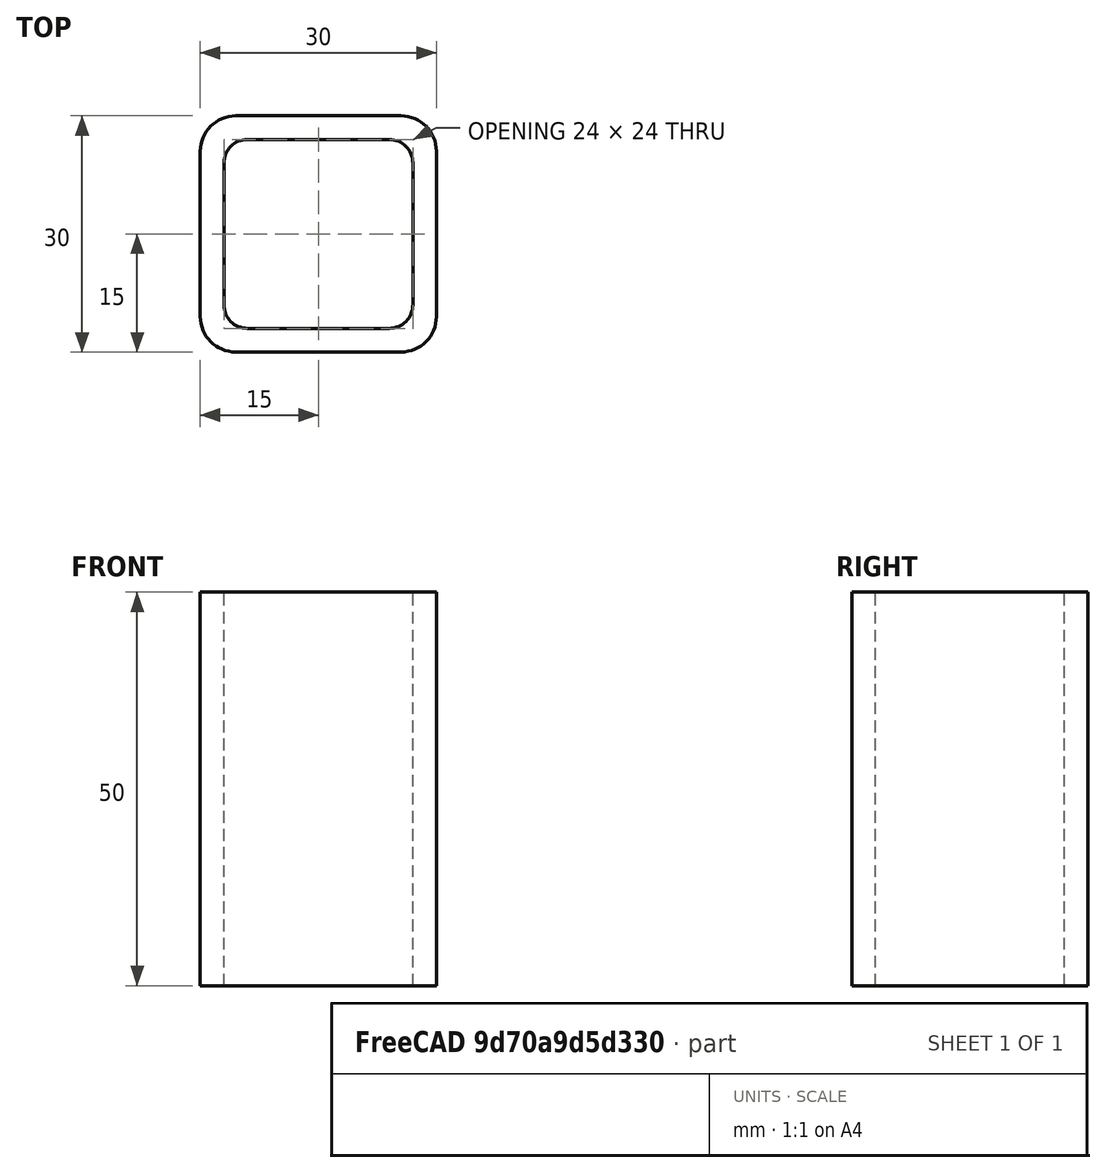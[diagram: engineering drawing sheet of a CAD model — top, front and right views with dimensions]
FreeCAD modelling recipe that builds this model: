
FCSTD DOCUMENT  (FreeCAD 0.15R4671 (Git))
Label: Square hollow section 30x30x3 EN10219 S235JRH
License: All rights reserved
LicenseURL: http://en.wikipedia.org/wiki/All_rights_reserved
objects: Sketcher::SketchObject×1, Part::Extrusion×1
note: 2 computed .brp shape members not serialized (recipe doc carries the construction recipe); baked Part::Feature solids carry a one-line shape summary decoded from their .brp

FEATURE [Sketcher::SketchObject] Sketch
  sketch-geometry (16):
    g0: LineSegment StartX=-9 StartY=12 StartZ=0 EndX=9 EndY=12 EndZ=0
    g1: LineSegment StartX=12 StartY=9 StartZ=0 EndX=12 EndY=-9 EndZ=0
    g2: LineSegment StartX=9 StartY=-12 StartZ=0 EndX=-9 EndY=-12 EndZ=0
    g3: LineSegment StartX=-12 StartY=-9 StartZ=0 EndX=-12 EndY=9 EndZ=0
    g4: LineSegment StartX=-10.5 StartY=15 StartZ=0 EndX=10.5 EndY=15 EndZ=0
    g5: LineSegment StartX=15 StartY=10.5 StartZ=0 EndX=15 EndY=-10.5 EndZ=0
    g6: LineSegment StartX=10.5 StartY=-15 StartZ=0 EndX=-10.5 EndY=-15 EndZ=0
    g7: LineSegment StartX=-15 StartY=-10.5 StartZ=0 EndX=-15 EndY=10.5 EndZ=0
    g8: ArcOfCircle CenterX=-9 CenterY=9 CenterZ=0 NormalX=0 NormalY=0 NormalZ=1 Radius=3 StartAngle=1.5708 EndAngle=3.14159
    g9: ArcOfCircle CenterX=9 CenterY=9 CenterZ=0 NormalX=0 NormalY=0 NormalZ=1 Radius=3 StartAngle=0 EndAngle=1.5708
    g10: ArcOfCircle CenterX=9 CenterY=-9 CenterZ=0 NormalX=0 NormalY=0 NormalZ=1 Radius=3 StartAngle=4.71239 EndAngle=6.28319
    g11: ArcOfCircle CenterX=-9 CenterY=-9 CenterZ=0 NormalX=0 NormalY=0 NormalZ=1 Radius=3 StartAngle=3.14159 EndAngle=4.71239
    g12: ArcOfCircle CenterX=10.5 CenterY=10.5 CenterZ=0 NormalX=0 NormalY=0 NormalZ=1 Radius=4.5 StartAngle=0 EndAngle=1.5708
    g13: ArcOfCircle CenterX=10.5 CenterY=-10.5 CenterZ=0 NormalX=0 NormalY=0 NormalZ=1 Radius=4.5 StartAngle=4.71239 EndAngle=6.28319
    g14: ArcOfCircle CenterX=-10.5 CenterY=-10.5 CenterZ=0 NormalX=0 NormalY=0 NormalZ=1 Radius=4.5 StartAngle=3.14159 EndAngle=4.71239
    g15: ArcOfCircle CenterX=-10.5 CenterY=10.5 CenterZ=0 NormalX=0 NormalY=0 NormalZ=1 Radius=4.5 StartAngle=1.5708 EndAngle=3.14159
  constraints (36):
    c: Horizontal(g2)
    c: Vertical(g3)
    c: Horizontal(g6)
    c: Vertical(g7)
    c: Tangent(g3,g8) = 1.5708
    c: Tangent(g0,g8) = 1.5708
    c: Tangent(g0,g9) = 1.5708
    c: Tangent(g1,g9) = 1.5708
    c: Tangent(g1,g10) = 1.5708
    c: Tangent(g2,g10) = 1.5708
    c: Tangent(g2,g11) = 1.5708
    c: Tangent(g3,g11) = 1.5708
    c: Tangent(g4,g12) = 1.5708
    c: Tangent(g5,g12) = 1.5708
    c: Tangent(g5,g13) = 1.5708
    c: Tangent(g6,g13) = 1.5708
    c: Tangent(g6,g14) = 1.5708
    c: Tangent(g7,g14) = 1.5708
    c: Tangent(g7,g15) = 1.5708
    c: Tangent(g4,g15) = 1.5708
    c: Equal(g9,g8)
    c: Equal(g9,g11)
    c: Equal(g9,g10)
    c: Equal(g12,g15)
    c: Equal(g12,g14)
    c: Equal(g12,g13)
    c: Symmetric(g4,g6,g-1)
    c: Symmetric(g7,g5,g-2)
    c: DistanceY(g4,g6) = -30
    c: DistanceX(g7,g5) = 30
    c: Symmetric(g3,g1,g-2)
    c: Symmetric(g0,g2,g-1)
    c: DistanceY(g0,g4) = 3
    c: DistanceX(g5,g1) = -3
    c: Radius(g9) = 3
    c: Radius(g12) = 4.5
FEATURE [Part::Extrusion] Extrude  label="Square hollow section 30x30x3 EN10219 S235JRH"
  Base = -> Sketch
  Dir = (0,0,50)
  Solid = true
